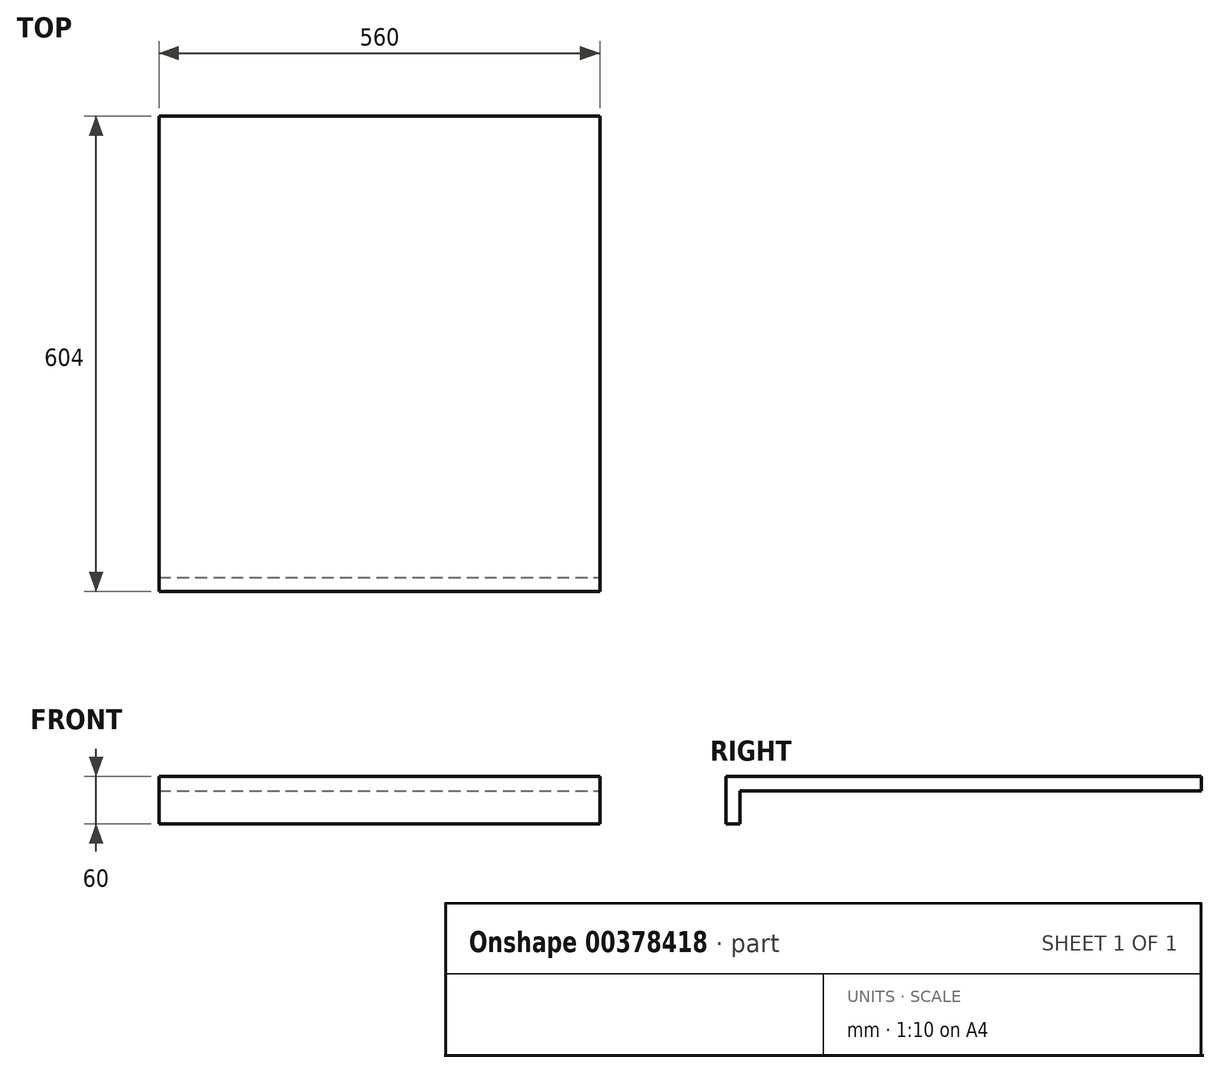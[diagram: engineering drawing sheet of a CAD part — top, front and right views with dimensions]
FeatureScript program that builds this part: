
annotation { "Feature Type Name" : "Feature", "Feature Type Description" : "" }
export const myFeature = defineFeature(function(context is Context, id is Id, definition is map)
    precondition{}
    {
        {
            var Q0;
            Q0=qCreatedBy(makeId("Top.planeOp"),FACE);
            var sketch = newSketch(context, id + "F0", { "sketchPlane" : qUnion([Q0])});
            skLineSegment(sketch, "E0.bottom", {"start": v(280, 302) * mm, "end": v(-280, 302) * mm});
            skLineSegment(sketch, "E0.top", {"start": v(280, -302) * mm, "end": v(-280, -302) * mm});
            skLineSegment(sketch, "E0.left", {"start": v(280, 302) * mm, "end": v(280, -302) * mm});
            skLineSegment(sketch, "E0.right", {"start": v(-280, 302) * mm, "end": v(-280, -302) * mm});
            skPoint(sketch, "E0.middle", {"position": v(0, 0) * mm});
            skSolve(sketch);
        }
        {
            var Q0;
            Q0 = qSketchRegion(id + "F0", true);
            extrude(context, id + "F1", {"entities" : qUnion([Q0]), "depth" : 18 * mm});
        }
        {
            var Q0;
            Q0=makeQuery(id+"F1.opExtrude","CAP_FACE",FACE,{"disambiguationData":[OSD([sQuery(id+"F0.wireOp",EDGE,"E0.bottom"),sQuery(id+"F0.wireOp",EDGE,"E0.top"),sQuery(id+"F0.wireOp",EDGE,"E0.left"),sQuery(id+"F0.wireOp",EDGE,"E0.right")])],"isStart":true});
            var sketch = newSketch(context, id + "F2", { "sketchPlane" : qUnion([Q0])});
            skLineSegment(sketch, "E1.bottom", {"start": v(-280, 302) * mm, "end": v(280, 302) * mm});
            skLineSegment(sketch, "E1.top", {"start": v(-280, 284) * mm, "end": v(280, 284) * mm});
            skLineSegment(sketch, "E1.left", {"start": v(-280, 302) * mm, "end": v(-280, 284) * mm});
            skLineSegment(sketch, "E1.right", {"start": v(280, 302) * mm, "end": v(280, 284) * mm});
            skSolve(sketch);
        }
        {
            var Q0;
            Q0 = qSketchRegion(id + "F2", true);
            extrude(context, id + "F3", {"entities" : qUnion([Q0]), "operationType" : NewBodyOperationType.ADD, "depth" : 42 * mm});
        }
    });
